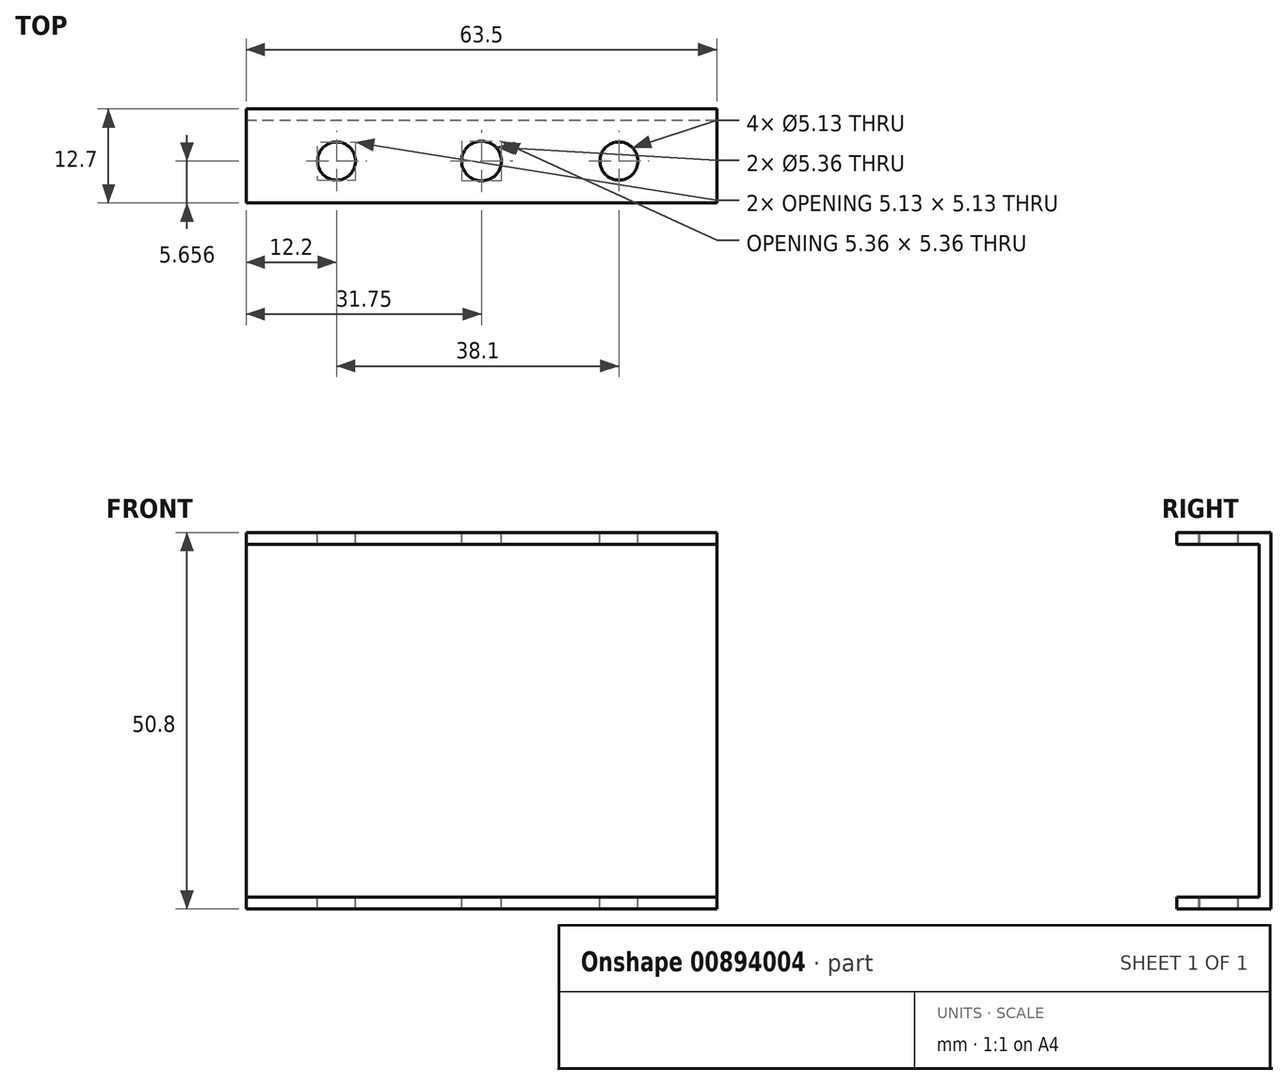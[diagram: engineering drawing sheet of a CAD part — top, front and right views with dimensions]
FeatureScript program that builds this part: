
annotation { "Feature Type Name" : "Feature", "Feature Type Description" : "" }
export const myFeature = defineFeature(function(context is Context, id is Id, definition is map)
    precondition{}
    {
        {
            var Q0;
            Q0=qCreatedBy(makeId("Right.planeOp"),FACE);
            var sketch = newSketch(context, id + "F0", { "sketchPlane" : qUnion([Q0])});
            skLineSegment(sketch, "E0", {"start": v(-0.8, 0) * mm, "end": v(0, 0) * mm});
            skLineSegment(sketch, "E1", {"start": v(0, 0) * mm, "end": v(0.8, 0) * mm});
            skLineSegment(sketch, "E2", {"start": v(0.8, 0) * mm, "end": v(0.8, 25.4) * mm});
            skLineSegment(sketch, "E3", {"start": v(0.8, 25.4) * mm, "end": v(-11.9, 25.4) * mm});
            skLineSegment(sketch, "E4", {"start": v(-11.9, 25.4) * mm, "end": v(-11.9, 23.81) * mm});
            skLineSegment(sketch, "E5", {"start": v(-11.9, 23.81) * mm, "end": v(-0.8, 23.81) * mm});
            skLineSegment(sketch, "E6", {"start": v(-0.8, 23.81) * mm, "end": v(-0.8, 0) * mm});
            skLineSegment(sketch, "E7.MirrorCS", {"start": v(0.8, -25.4) * mm, "end": v(-11.9, -25.4) * mm});
            skLineSegment(sketch, "E8.MirrorCS", {"start": v(-11.9, -23.81) * mm, "end": v(-0.8, -23.81) * mm});
            skLineSegment(sketch, "E9.MirrorCS", {"start": v(-11.9, -25.4) * mm, "end": v(-11.9, -23.81) * mm});
            skLineSegment(sketch, "E10.MirrorCS", {"start": v(-0.8, -23.81) * mm, "end": v(-0.8, 0) * mm});
            skLineSegment(sketch, "E11.MirrorCS", {"start": v(0.8, 0) * mm, "end": v(0.8, -25.4) * mm});
            skSolve(sketch);
        }
        {
            var Q0;
            Q0 = qSketchRegion(id + "F0", true);
            extrude(context, id + "F1", {"entities" : qUnion([Q0]), "endBound" : BoundingType.SYMMETRIC, "depth" : 63.5 * mm, "offsetDistance" : 25.4 * mm});
        }
        {
            var Q0;
            Q0=qCreatedBy(makeId("Top.planeOp"),FACE);
            var sketch = newSketch(context, id + "F2", { "sketchPlane" : qUnion([Q0])});
            skCircle(sketch, "E12", {"center": v(0, -6.25) * mm, "radius": 2.68 * mm});
            skCircle(sketch, "E13", {"center": v(18.55, -6.25) * mm, "radius": 2.57 * mm});
            skCircle(sketch, "E14", {"center": v(-19.55, -6.25) * mm, "radius": 2.57 * mm});
            skSolve(sketch);
        }
        {
            var Q0;
            Q0 = qSketchRegion(id + "F2", true);
            extrude(context, id + "F3", {"entities" : qUnion([Q0]), "operationType" : NewBodyOperationType.REMOVE, "endBound" : BoundingType.THROUGH_ALL, "oppositeDirection" : true, "depth" : 25.4 * mm, "offsetDistance" : 25.4 * mm, "hasSecondDirection" : true, "secondDirectionBound" : SecondDirectionBoundingType.THROUGH_ALL, "secondDirectionOppositeDirection" : false, "secondDirectionDepth" : 25.4 * mm});
        }
    });
